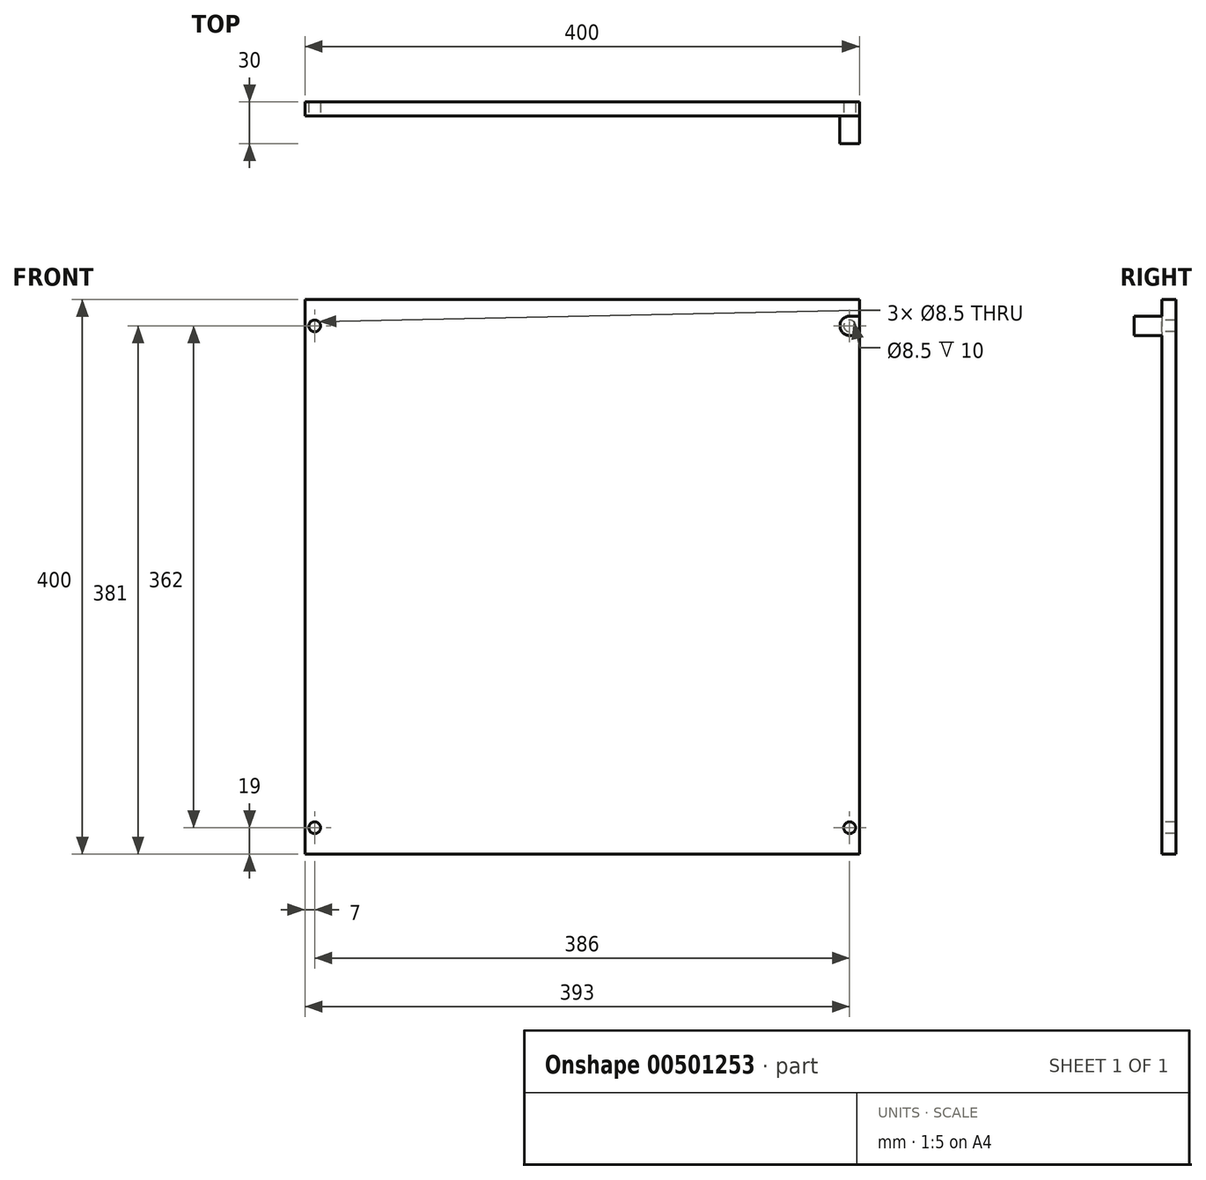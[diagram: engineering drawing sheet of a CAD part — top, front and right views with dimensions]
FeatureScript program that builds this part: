
annotation { "Feature Type Name" : "Feature", "Feature Type Description" : "" }
export const myFeature = defineFeature(function(context is Context, id is Id, definition is map)
    precondition{}
    {
        {
            var Q0;
            Q0=qCreatedBy(makeId("Front.planeOp"),FACE);
            var sketch = newSketch(context, id + "F0", { "sketchPlane" : qUnion([Q0])});
            skLineSegment(sketch, "E0.bottom", {"start": v(0, 0) * mm, "end": v(400, 0) * mm});
            skLineSegment(sketch, "E0.top", {"start": v(0, 400) * mm, "end": v(400, 400) * mm});
            skLineSegment(sketch, "E0.left", {"start": v(0, 0) * mm, "end": v(0, 400) * mm});
            skLineSegment(sketch, "E0.right", {"start": v(400, 0) * mm, "end": v(400, 400) * mm});
            skSolve(sketch);
        }
        {
            var Q0;
            Q0=makeQuery(id+"F0.imprint","IMPRINT",FACE,{"disambiguationData":[TD([[makeQuery(id+"F0.imprint","IMPRINT",EDGE,{"derivedFrom":sQuery(id+"F0.wireOp",EDGE,"E0.bottom")}),1.0]])]});
            extrude(context, id + "F1", {"entities" : qUnion([Q0]), "depth" : 30 * mm});
        }
        {
            var Q0;
            Q0=makeQuery(id+"F1.opExtrude","CAP_FACE",FACE,{"disambiguationData":[OSD([sQuery(id+"F0.wireOp",EDGE,"E0.bottom"),sQuery(id+"F0.wireOp",EDGE,"E0.top"),sQuery(id+"F0.wireOp",EDGE,"E0.left"),sQuery(id+"F0.wireOp",EDGE,"E0.right")])],"isStart":false});
            var sketch = newSketch(context, id + "F2", { "sketchPlane" : qUnion([Q0])});
            skLineSegment(sketch, "E1", {"start": v(0, 200) * mm, "end": v(0, 381) * mm});
            skArc(sketch, "E2", {"start": v(7, 374) * mm, "mid": v(14, 381) * mm, "end": v(7, 388) * mm});
            skLineSegment(sketch, "E3", {"start": v(7, 388) * mm, "end": v(0, 388) * mm});
            skLineSegment(sketch, "E4.MirrorCS", {"start": v(7, 374) * mm, "end": v(0, 374) * mm});
            skLineSegment(sketch, "E5", {"start": v(0, 200) * mm, "end": v(39.65, 200) * mm});
            skLineSegment(sketch, "E6.MirrorCS", {"start": v(7, 26) * mm, "end": v(0, 26) * mm});
            skLineSegment(sketch, "E7.MirrorCS", {"start": v(7, 12) * mm, "end": v(0, 12) * mm});
            skArc(sketch, "E8.MirrorCS", {"start": v(7, 26) * mm, "mid": v(14, 19) * mm, "end": v(7, 12) * mm});
            skLineSegment(sketch, "E9", {"start": v(200, 400) * mm, "end": v(200, 341.94) * mm});
            skPoint(sketch, "E9.endSnap0", {"position": v(200, 400) * mm});
            skArc(sketch, "E10.MirrorCS", {"start": v(393, 374) * mm, "mid": v(386, 381) * mm, "end": v(393, 388) * mm});
            skLineSegment(sketch, "E11.MirrorCS", {"start": v(393, 374) * mm, "end": v(400, 374) * mm});
            skLineSegment(sketch, "E12.MirrorCS", {"start": v(393, 388) * mm, "end": v(400, 388) * mm});
            skLineSegment(sketch, "E13.MirrorCS", {"start": v(393, 12) * mm, "end": v(400, 12) * mm});
            skLineSegment(sketch, "E14.MirrorCS", {"start": v(393, 26) * mm, "end": v(400, 26) * mm});
            skArc(sketch, "E15.MirrorCS", {"start": v(393, 26) * mm, "mid": v(386, 19) * mm, "end": v(393, 12) * mm});
            skSolve(sketch);
        }
        {
            var Q0;
            Q0=qSketchRegion(id+"F2",true);
            var Q1;
            {var subQ0=sQuery(id+"F2.wireOp",EDGE,"E6.MirrorCS");Q1=makeQuery(id+"F2.imprint","IMPRINT",FACE,{"disambiguationData":[TD([[makeQuery(id+"F2.imprint","IMPRINT",EDGE,{"derivedFrom":subQ0}),1.0]])]});}
            var Q2;
            {var subQ0=sQuery(id+"F2.wireOp",EDGE,"E13.MirrorCS");Q2=makeQuery(id+"F2.imprint","IMPRINT",FACE,{"disambiguationData":[TD([[makeQuery(id+"F2.imprint","IMPRINT",EDGE,{"derivedFrom":subQ0}),1.0]])]});}
            var Q3;
            Q3=makeQuery(id+"F2.imprint","IMPRINT",FACE,{"disambiguationData":[TD([[makeQuery(id+"F2.imprint","IMPRINT",EDGE,{"derivedFrom":sQuery(id+"F2.wireOp",EDGE,"E10.MirrorCS")}),-1.0]])]});
            var Q4;
            Q4=makeQuery(id+"F2.imprint","IMPRINT",FACE,{"disambiguationData":[TD([[makeQuery(id+"F2.imprint","IMPRINT",EDGE,{"derivedFrom":sQuery(id+"F2.wireOp",EDGE,"E2")}),1.0]])]});
            extrude(context, id + "F3", {"entities" : qUnion([Q0, Q1, Q2, Q3, Q4]), "operationType" : NewBodyOperationType.REMOVE, "oppositeDirection" : true, "depth" : 20 * mm});
        }
        {
            var Q0;
            Q0=makeQuery(id+"F3.boolean.opBoolean","COPY",FACE,{"derivedFrom":makeQuery(id+"F3.opExtrude","CAP_FACE",FACE,{"disambiguationData":[OSD([sQuery(id+"F0.wireOp",EDGE,"E0.left"),sQuery(id+"F2.wireOp",EDGE,"E6.MirrorCS"),sQuery(id+"F2.wireOp",EDGE,"E7.MirrorCS"),sQuery(id+"F2.wireOp",EDGE,"E8.MirrorCS")])],"isStart":false})});
            var sketch = newSketch(context, id + "F4", { "sketchPlane" : qUnion([Q0])});
            skCircle(sketch, "E16", {"center": v(7, 19) * mm, "radius": 4.25 * mm});
            skCircle(sketch, "E17.0.1.0", {"center": v(7, 381) * mm, "radius": 4.25 * mm});
            skCircle(sketch, "E17.1.0.0", {"center": v(393, 19) * mm, "radius": 4.25 * mm});
            skCircle(sketch, "E17.1.1.0", {"center": v(393, 381) * mm, "radius": 4.25 * mm});
            skLineSegment(sketch, "E17.direction1", {"start": v(7, 19) * mm, "end": v(393, 19) * mm, "construction": true});
            skLineSegment(sketch, "E17.direction2", {"start": v(7, 19) * mm, "end": v(7, 381) * mm, "construction": true});
            skSolve(sketch);
        }
        {
            var Q0;
            Q0=sQuery(id+"F4.wireOp",VERTEX,"E17.direction2.end");
            var Q1;
            Q1=sQuery(id+"F4.wireOp",VERTEX,"E17.1.1.0.center");
            var Q2;
            Q2=sQuery(id+"F4.wireOp",VERTEX,"E17.1.0.0.center");
            var Q3;
            Q3=sQuery(id+"F4.wireOp",VERTEX,"E16.center");
            var Q4;
            Q4=makeQuery(id+"F1.opExtrude","SWEPT_BODY",BODY,{"disambiguationData":[OSD([sQuery(id+"F0.wireOp",EDGE,"E0.bottom"),sQuery(id+"F0.wireOp",EDGE,"E0.top"),sQuery(id+"F0.wireOp",EDGE,"E0.left"),sQuery(id+"F0.wireOp",EDGE,"E0.right")])]});
            hole(context, id + "F5", {"style" : HoleStyle.SIMPLE, "endStyle" : HoleEndStyle.THROUGH, "holeDiameter" : 8.5 * mm, "isTappedThrough" : true, "tappedDepth" : 12 * mm, "tapClearance" : 3, "locations" : qUnion([Q0, Q1, Q2, Q3]), "scope" : qUnion([Q4])});
        }
    });
